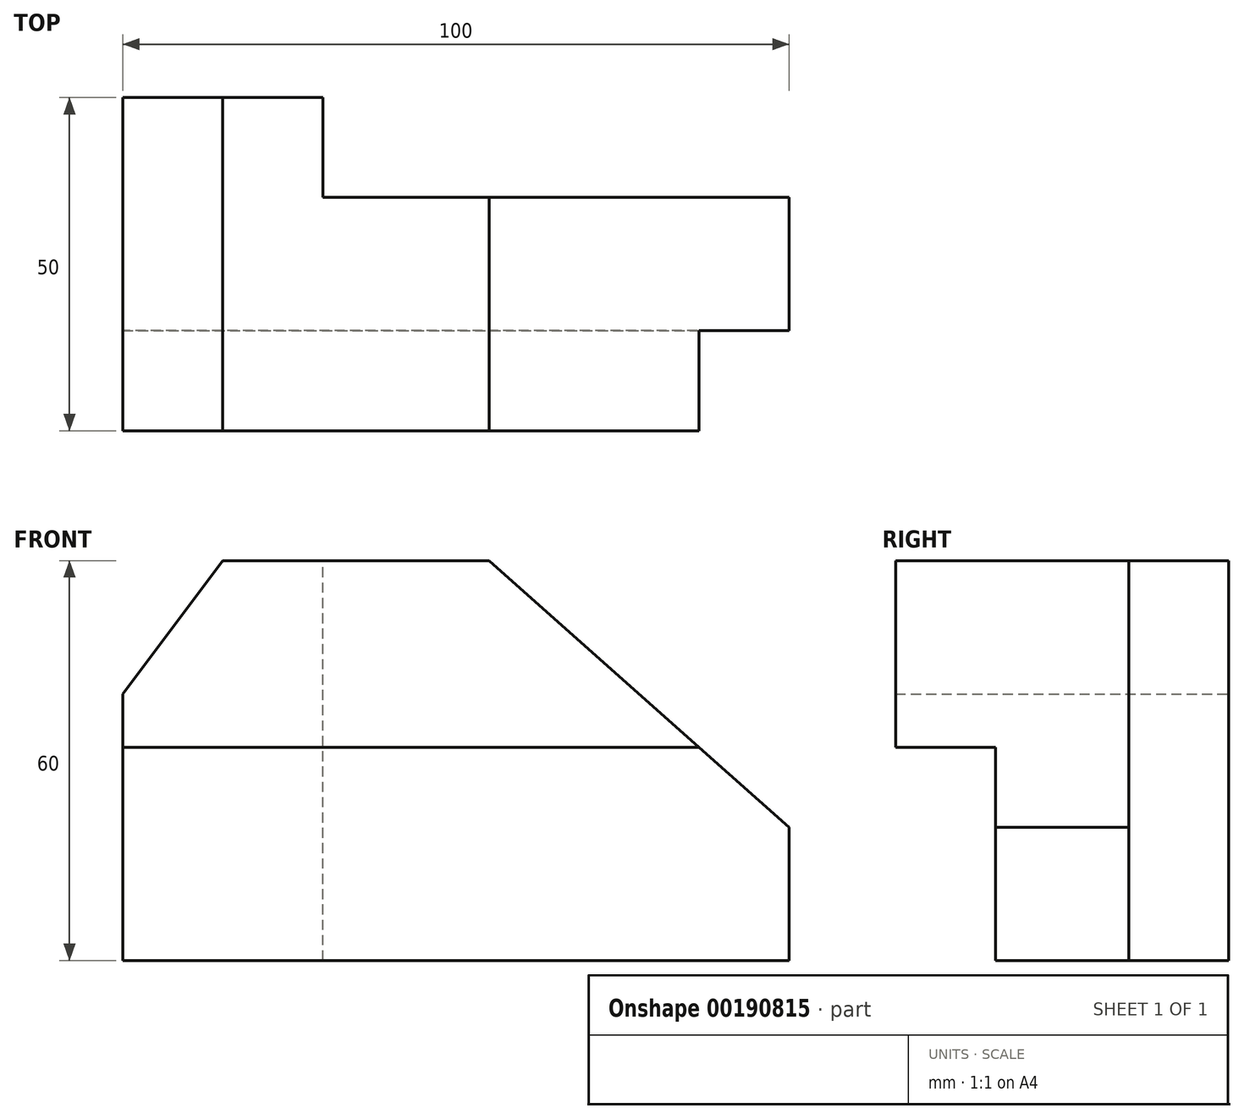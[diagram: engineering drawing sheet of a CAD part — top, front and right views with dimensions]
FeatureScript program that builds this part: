
annotation { "Feature Type Name" : "Feature", "Feature Type Description" : "" }
export const myFeature = defineFeature(function(context is Context, id is Id, definition is map)
    precondition{}
    {
        {
            var Q0;
            Q0=qCreatedBy(makeId("Front.planeOp"),FACE);
            var sketch = newSketch(context, id + "F0", { "sketchPlane" : qUnion([Q0])});
            skLineSegment(sketch, "E0", {"start": v(0, 0) * mm, "end": v(0, 40) * mm});
            skLineSegment(sketch, "E1", {"start": v(0, 40) * mm, "end": v(15, 60) * mm});
            skLineSegment(sketch, "E2", {"start": v(15, 60) * mm, "end": v(55, 60) * mm});
            skLineSegment(sketch, "E3", {"start": v(55, 60) * mm, "end": v(100, 20) * mm});
            skLineSegment(sketch, "E4", {"start": v(100, 20) * mm, "end": v(100, 0) * mm});
            skLineSegment(sketch, "E5", {"start": v(100, 0) * mm, "end": v(0, 0) * mm});
            skSolve(sketch);
        }
        {
            var Q0;
            Q0 = qSketchRegion(id + "F0", true);
            extrude(context, id + "F1", {"entities" : qUnion([Q0]), "depth" : 50 * mm});
        }
        {
            var Q0;
            Q0=makeQuery(id+"F1.opExtrude","CAP_FACE",FACE,{"disambiguationData":[OSD([sQuery(id+"F0.wireOp",EDGE,"E0"),sQuery(id+"F0.wireOp",EDGE,"E1"),sQuery(id+"F0.wireOp",EDGE,"E2"),sQuery(id+"F0.wireOp",EDGE,"E3"),sQuery(id+"F0.wireOp",EDGE,"E4"),sQuery(id+"F0.wireOp",EDGE,"E5")])],"isStart":false});
            var sketch = newSketch(context, id + "F2", { "sketchPlane" : qUnion([Q0])});
            skLineSegment(sketch, "E6.bottom", {"start": v(0, 0) * mm, "end": v(100, 0) * mm});
            skLineSegment(sketch, "E6.top", {"start": v(0, 32) * mm, "end": v(100, 32) * mm});
            skLineSegment(sketch, "E6.left", {"start": v(0, 0) * mm, "end": v(0, 32) * mm});
            skLineSegment(sketch, "E6.right", {"start": v(100, 0) * mm, "end": v(100, 32) * mm});
            skSolve(sketch);
        }
        {
            var Q0;
            Q0 = qSketchRegion(id + "F2", true);
            extrude(context, id + "F3", {"entities" : qUnion([Q0]), "operationType" : NewBodyOperationType.REMOVE, "oppositeDirection" : true, "depth" : 15 * mm});
        }
        {
            var Q0;
            Q0=makeQuery(id+"F1.opExtrude","CAP_FACE",FACE,{"disambiguationData":[OSD([sQuery(id+"F0.wireOp",EDGE,"E0"),sQuery(id+"F0.wireOp",EDGE,"E1"),sQuery(id+"F0.wireOp",EDGE,"E2"),sQuery(id+"F0.wireOp",EDGE,"E3"),sQuery(id+"F0.wireOp",EDGE,"E4"),sQuery(id+"F0.wireOp",EDGE,"E5")])],"isStart":true});
            var sketch = newSketch(context, id + "F4", { "sketchPlane" : qUnion([Q0])});
            skLineSegment(sketch, "E7.bottom", {"start": v(-100, 0) * mm, "end": v(-30, 0) * mm});
            skLineSegment(sketch, "E7.top", {"start": v(-100, 60) * mm, "end": v(-30, 60) * mm});
            skLineSegment(sketch, "E7.left", {"start": v(-100, 0) * mm, "end": v(-100, 60) * mm});
            skLineSegment(sketch, "E7.right", {"start": v(-30, 0) * mm, "end": v(-30, 60) * mm});
            skSolve(sketch);
        }
        {
            var Q0;
            Q0 = qSketchRegion(id + "F4", true);
            extrude(context, id + "F5", {"entities" : qUnion([Q0]), "operationType" : NewBodyOperationType.REMOVE, "oppositeDirection" : true, "depth" : 15 * mm});
        }
    });
